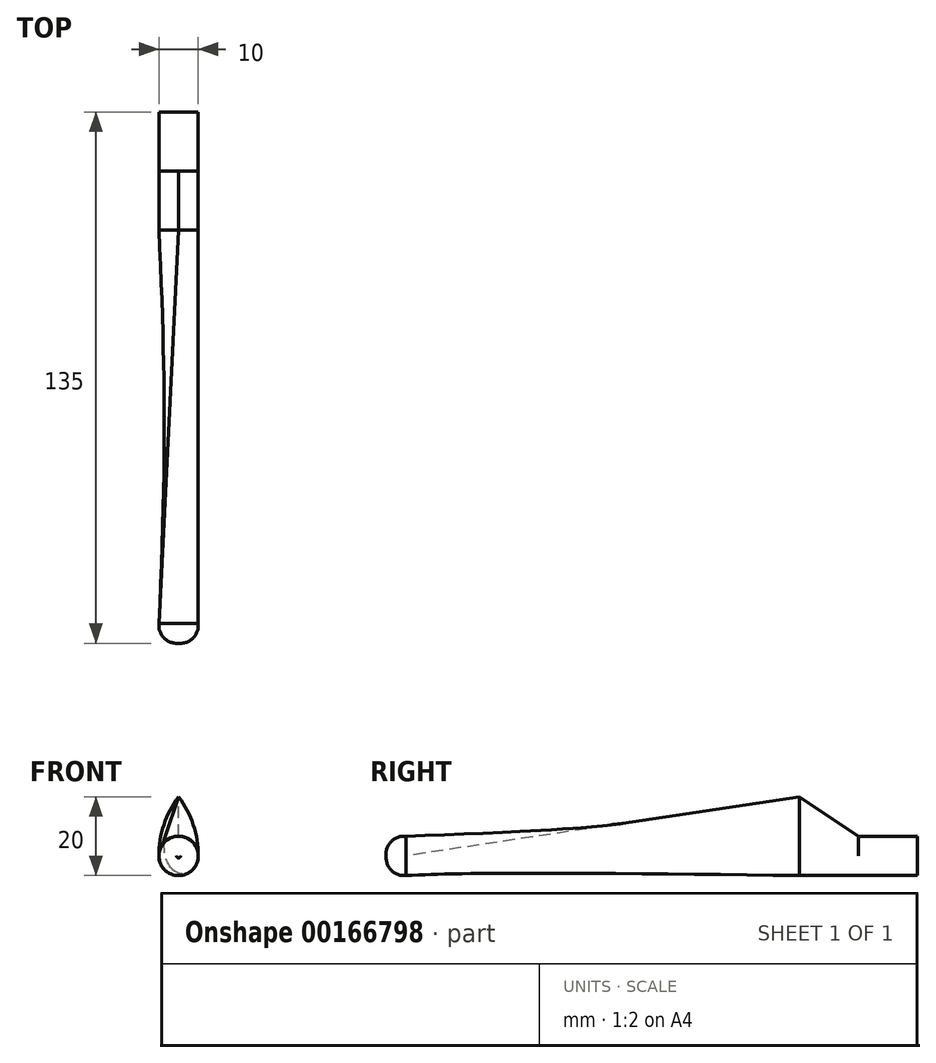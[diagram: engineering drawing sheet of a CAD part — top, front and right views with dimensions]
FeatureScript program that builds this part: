
annotation { "Feature Type Name" : "Feature", "Feature Type Description" : "" }
export const myFeature = defineFeature(function(context is Context, id is Id, definition is map)
    precondition{}
    {
        {
            var Q0;
            Q0=qCreatedBy(makeId("Front.planeOp"),FACE);
            var sketch = newSketch(context, id + "F0", { "sketchPlane" : qUnion([Q0])});
            skCircle(sketch, "E0", {"center": v(0, 0) * mm, "radius": 5 * mm});
            skSolve(sketch);
        }
        {
            var Q0;
            Q0=makeQuery(id+"F0.imprint","IMPRINT",FACE,{"disambiguationData":[TD([[makeQuery(id+"F0.imprint","IMPRINT",EDGE,{"derivedFrom":sQuery(id+"F0.wireOp",EDGE,"E0")}),1.0]])]});
            extrude(context, id + "F1", {"entities" : qUnion([Q0]), "depth" : 15 * mm});
        }
        {
            var Q0;
            Q0=makeQuery(id+"F1.opExtrude","CAP_FACE",FACE,{"disambiguationData":[OSD([sQuery(id+"F0.wireOp",EDGE,"E0")])],"isStart":false});
            var sketch = newSketch(context, id + "F2", { "sketchPlane" : qUnion([Q0])});
            skCircle(sketch, "E1.0.0", {"center": v(0, 0) * mm, "radius": 5 * mm});
            skSolve(sketch);
        }
        {
            var Q0;
            Q0=makeQuery(id+"F2.imprint","IMPRINT",FACE,{"disambiguationData":[TD([[makeQuery(id+"F2.imprint","IMPRINT",EDGE,{"derivedFrom":sQuery(id+"F2.wireOp",EDGE,"E1.0.0")}),1.0]])]});
            cPlane(context, id + "F3", {"entities" : qUnion([Q0]), "cplaneType" : CPlaneType.OFFSET, "offset" : 15 * mm, "width" : 150 * mm, "height" : 150 * mm});
        }
        {
            var Q0;
            Q0=qCreatedBy(id+"F3.planeOp",FACE);
            var sketch = newSketch(context, id + "F4", { "sketchPlane" : qUnion([Q0])});
            skArc(sketch, "E2", {"start": v(0, -5) * mm, "mid": v(3.54, -3.54) * mm, "end": v(5, 0) * mm});
            skArc(sketch, "E3", {"start": v(-5, 0) * mm, "mid": v(-3.54, -3.54) * mm, "end": v(0, -5) * mm});
            skArc(sketch, "E4", {"start": v(0, 15) * mm, "mid": v(-3.74, 7.91) * mm, "end": v(-5, 0) * mm});
            skArc(sketch, "E5.MirrorCS", {"start": v(0, 15) * mm, "mid": v(3.74, 7.91) * mm, "end": v(5, 0) * mm});
            skSolve(sketch);
        }
        {
            var Q1;
            Q1=makeQuery(id+"F2.imprint","IMPRINT",FACE,{"disambiguationData":[TD([[makeQuery(id+"F2.imprint","IMPRINT",EDGE,{"derivedFrom":sQuery(id+"F2.wireOp",EDGE,"E1.0.0")}),1.0]])]});
            var Q2;
            Q2=makeQuery(id+"F4.imprint","IMPRINT",FACE,{"disambiguationData":[TD([[makeQuery(id+"F4.imprint","IMPRINT",EDGE,{"derivedFrom":sQuery(id+"F4.wireOp",EDGE,"E2")}),1.0]])]});
            loft(context, id + "F5", {"operationType" : NewBodyOperationType.ADD, "sheetProfilesArray" : [{ "sheetProfileEntities" : qUnion([Q1]) }, { "sheetProfileEntities" : qUnion([Q2]) }]});
        }
        {
            var Q0;
            Q0=makeQuery(id+"F5.opLoft","CAP_FACE",FACE,{"disambiguationData":[OSD([makeQuery(id+"F4.imprint","IMPRINT",FACE,{"disambiguationData":[TD([[makeQuery(id+"F4.imprint","IMPRINT",EDGE,{"derivedFrom":sQuery(id+"F4.wireOp",EDGE,"E2")}),1.0]])]})])],"isStart":true});
            cPlane(context, id + "F6", {"entities" : qUnion([Q0]), "cplaneType" : CPlaneType.OFFSET, "offset" : 100 * mm, "width" : 150 * mm, "height" : 150 * mm});
        }
        {
            var Q0;
            Q0=qCreatedBy(id+"F6.planeOp",FACE);
            var sketch = newSketch(context, id + "F7", { "sketchPlane" : qUnion([Q0])});
            skArc(sketch, "E6.0", {"start": v(-5, 0) * mm, "mid": v(0, -5) * mm, "end": v(5, 0) * mm});
            skCircle(sketch, "E7", {"center": v(0, 0) * mm, "radius": 5 * mm});
            skSolve(sketch);
        }
        {
            var Q1;
            Q1=makeQuery(id+"F5.opLoft","CAP_FACE",FACE,{"disambiguationData":[OSD([makeQuery(id+"F4.imprint","IMPRINT",FACE,{"disambiguationData":[TD([[makeQuery(id+"F4.imprint","IMPRINT",EDGE,{"derivedFrom":sQuery(id+"F4.wireOp",EDGE,"E2")}),1.0]])]})])],"isStart":true});
            var Q2;
            Q2=makeQuery(id+"F7.imprint","IMPRINT",FACE,{"disambiguationData":[TD([[makeQuery(id+"F7.imprint","IMPRINT",EDGE,{"derivedFrom":sQuery(id+"F7.wireOp",EDGE,"E7")}),1.0]])]});
            loft(context, id + "F8", {"operationType" : NewBodyOperationType.ADD, "sheetProfilesArray" : [{ "sheetProfileEntities" : qUnion([Q1]) }, { "sheetProfileEntities" : qUnion([Q2]) }]});
        }
        {
            var Q0;
            Q0=makeQuery(id+"F8.opLoft","CAP_FACE",FACE,{"disambiguationData":[OSD([makeQuery(id+"F7.imprint","IMPRINT",FACE,{"disambiguationData":[TD([[makeQuery(id+"F7.imprint","IMPRINT",EDGE,{"derivedFrom":sQuery(id+"F7.wireOp",EDGE,"E7")}),1.0]])]})])],"isStart":true});
            extrude(context, id + "F9", {"entities" : qUnion([Q0]), "operationType" : NewBodyOperationType.ADD, "depth" : 5 * mm});
        }
        {
            var Q0;
            Q0=makeQuery(id+"F9.opExtrude","CAP_FACE",FACE,{"disambiguationData":[OSD([makeQuery(id+"F7.imprint","IMPRINT",FACE,{"disambiguationData":[TD([[makeQuery(id+"F7.imprint","IMPRINT",EDGE,{"derivedFrom":sQuery(id+"F7.wireOp",EDGE,"E7")}),1.0]])]})])],"isStart":false});
            fillet(context, id + "F10", {"entities" : qUnion([Q0]), "radius" : 4.5 * mm, "tangentPropagation" : true, "allowEdgeOverflow" : false});
        }
    });
